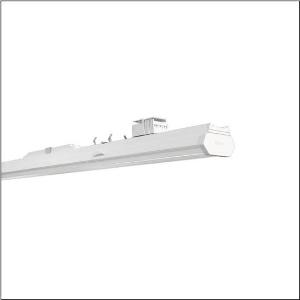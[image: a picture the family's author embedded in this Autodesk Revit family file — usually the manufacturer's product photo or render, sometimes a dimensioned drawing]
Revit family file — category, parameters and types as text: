
# Revit family: licross_r__21_protected_mo_52td12dn4a5gd_b3fc
name_source: partatom
category: Lighting Fixtures
units: mm (PartAtom-declared; Revit-internal decimal feet)

## family parameters
Cut with Voids When Loaded = No
Host = Face
Light Source = No
Part Type = Normal
Room Calculation Point = No
Round Connector Dimension = Use Diameter
Shared = No

## types (1)
- --- (1 x LED, 1610 lm, 10.2 W, 4000K)
    Apparent Load = 10 VA
    CIE Flux Codes = 73 92 98 99 100
    Color Rendering = 80
    Color Temperature = 4000K
    Default Elevation = 1800 mm
    Description = Licross® 21 Protected MO, luminaire insert, of sheet steel, galvanised, coil coated, white, length: 1.500mm, width: 90mm, height: 103mm, LED rated luminous flux: 10.700lm, light colour: 840, control gear: DALI 2, with plug, 6-pole, with phase selection, mains connection: 220..240V, AC/DC, 0/50..60Hz, rated input power: 62W, without changeover relay, for emergency light function, for central battery installations according to DIN EN 60598-2-22, halogen-free wiring, primary light control with lens, of plastic, primary optical cover: cover, of PMMA, light emission: direct distribution, primary light characteristic: symmetric, protection rating (complete): IP54, insulation class (complete): insulation class I (protective earthing), certification: CE, ENEC, VDE, UKCA, protection symbol: D if used in an environment with non-conductive dust loads with corresponding accessories, impact resistance: IK06, permissible ambient temperature for indoor applications: -25..+35°C, standard: EN 60598-2-22, corresponds to IFS (International Featured Standards) requirements for safety and quality in the food industry, reducing of maximum allowable ambient temperature of 5°C with ceiling mounting, LABS conformity tested according to VDMA 24364:2018-05, packaging unit: 1 piece
    Height = 92 mm
    Lamp = 1 x LED
    Lamp Light Flux = 1610 lm
    Lamp Power = 10.2 W
    Lamp count = 1
    Length = 1500 mm
    Luminous efficacy = 158 lm/W
    Manufacturer = Siteco
    ModVariant = No
    Model = 52TD12DN4A5GD
    Mounting Place = Ceiling
    Mounting Type = Pendant
    Number of Poles = 1
    OnlyDefault = Yes
    Power Factor = 1
    Product Name = Licross® 21 Protected MO
    Product group = luminaire insert
    ProductGroupID = 901
    Protection Class = Protection class I
    Protection Degree = IP 54
    RLX_Detail_Level = 1
    RLX_Emergency_Light_Flux = 0 lm
    RLX_Emergency_Type = 0
    RLX_Emergency_Type_DB = No
    RlxData = <blob elided: 24933 chars, md5=d033318a>
    Socket = socket
    Standby Power = 0 W
    System Light Flux = 1610 lm
    System Power = 10 W
    Type Comments = : DC mode (central or group accumulator) initial emergency light level
    Type Image = l_1256148.jpg
    URL = http://relux.com
    VarID = @adj_064457
    Voltage = 0 V
    Weight = 0.00 kg
    Width = 88 mm

## geometry (parser evidence)
native form markers: Blend x4, Sweep x9
no freeform markers — native parametric forms only
